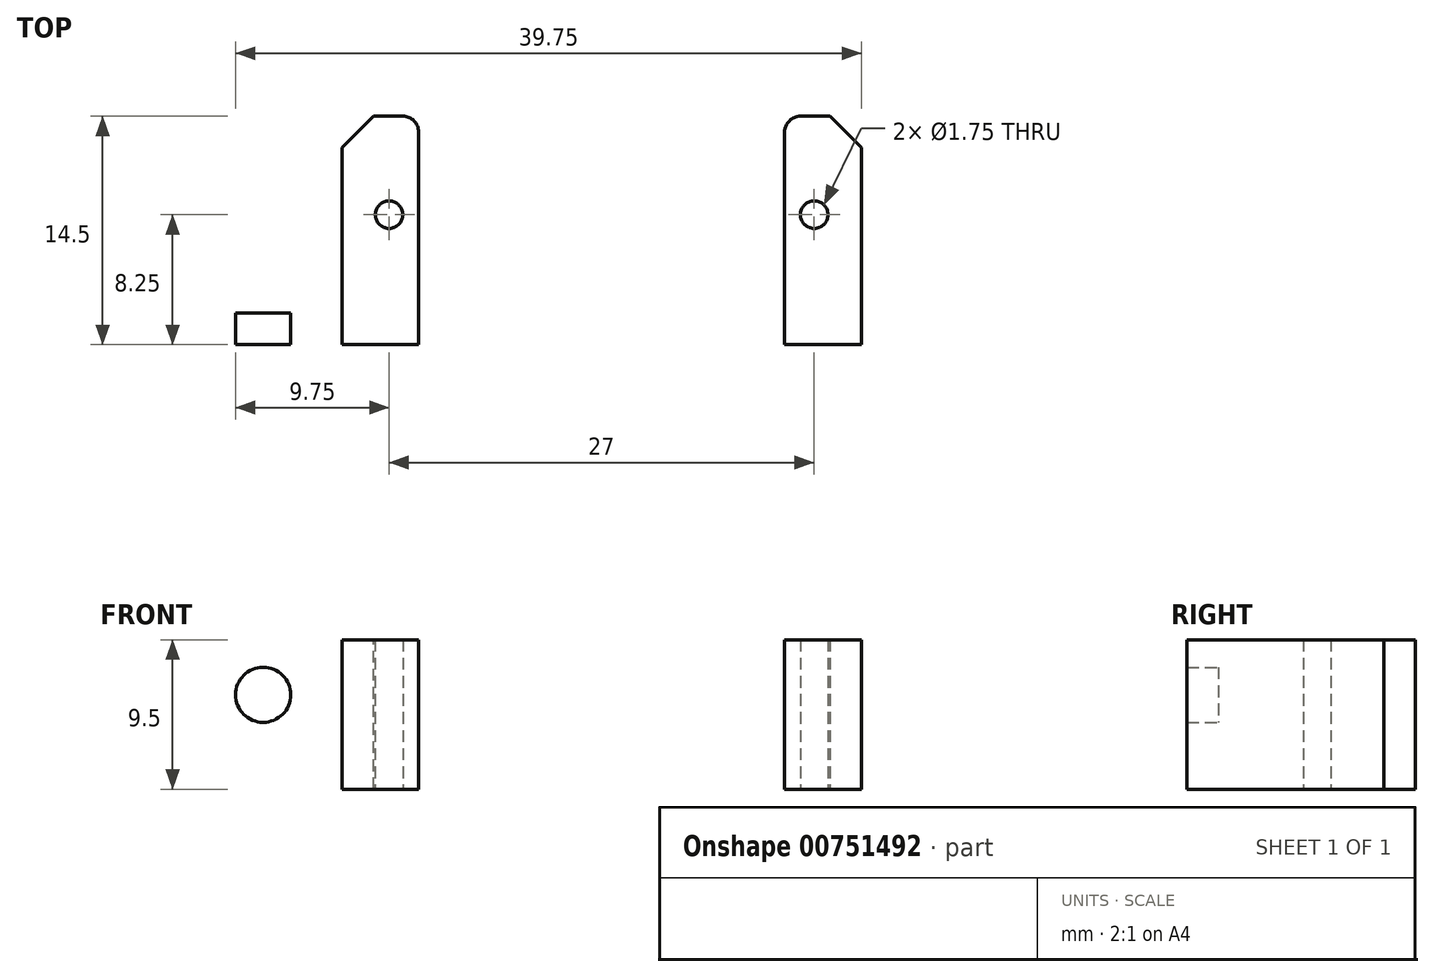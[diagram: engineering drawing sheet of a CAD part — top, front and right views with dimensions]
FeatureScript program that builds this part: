
annotation { "Feature Type Name" : "Feature", "Feature Type Description" : "" }
export const myFeature = defineFeature(function(context is Context, id is Id, definition is map)
    precondition{}
    {
        {
            var Q0;
            Q0=qCreatedBy(makeId("Top.planeOp"),FACE);
            var sketch = newSketch(context, id + "F0", { "sketchPlane" : qUnion([Q0])});
            skLineSegment(sketch, "E0.bottom", {"start": v(-16.5, 7.25) * mm, "end": v(16.5, 7.25) * mm});
            skLineSegment(sketch, "E0.top", {"start": v(-16.5, -7.25) * mm, "end": v(16.5, -7.25) * mm});
            skLineSegment(sketch, "E0.left", {"start": v(-16.5, 7.25) * mm, "end": v(-16.5, -7.25) * mm});
            skLineSegment(sketch, "E0.right", {"start": v(16.5, 7.25) * mm, "end": v(16.5, -7.25) * mm});
            skPoint(sketch, "E0.middle", {"position": v(0, 0) * mm});
            skLineSegment(sketch, "E1.bottom", {"start": v(-16.5, -5.25) * mm, "end": v(-24.5, -5.25) * mm});
            skLineSegment(sketch, "E1.top", {"start": v(-16.5, -7.25) * mm, "end": v(-24.5, -7.25) * mm});
            skLineSegment(sketch, "E1.left", {"start": v(-16.5, -5.25) * mm, "end": v(-16.5, -7.25) * mm});
            skLineSegment(sketch, "E1.right", {"start": v(-24.5, -5.25) * mm, "end": v(-24.5, -7.25) * mm});
            skLineSegment(sketch, "E2.MirrorCS", {"start": v(16.5, -5.25) * mm, "end": v(24.5, -5.25) * mm});
            skLineSegment(sketch, "E3.MirrorCS", {"start": v(16.5, -7.25) * mm, "end": v(24.5, -7.25) * mm});
            skLineSegment(sketch, "E4.MirrorCS", {"start": v(24.5, -5.25) * mm, "end": v(24.5, -7.25) * mm});
            skLineSegment(sketch, "E5.bottom", {"start": v(-11.62, 7.25) * mm, "end": v(11.62, 7.25) * mm});
            skLineSegment(sketch, "E5.top", {"start": v(-11.62, -5.25) * mm, "end": v(11.62, -5.25) * mm});
            skLineSegment(sketch, "E5.left", {"start": v(-11.62, 7.25) * mm, "end": v(-11.62, -5.25) * mm});
            skLineSegment(sketch, "E5.right", {"start": v(11.62, 7.25) * mm, "end": v(11.62, -5.25) * mm});
            skLineSegment(sketch, "E6", {"start": v(-11.62, -5.25) * mm, "end": v(-16.5, -5.25) * mm});
            skLineSegment(sketch, "E7", {"start": v(11.62, -5.25) * mm, "end": v(16.5, -5.25) * mm});
            skCircle(sketch, "E8", {"center": v(-13.5, 1) * mm, "radius": 0.88 * mm});
            skCircle(sketch, "E9.MirrorC", {"center": v(13.5, 1) * mm, "radius": 0.88 * mm});
            skSolve(sketch);
        }
        {
            var Q0;
            {var subQ1=sQuery(id+"F0.wireOp",EDGE,"E0.top");Q0=makeQuery(id+"F0.imprint","IMPRINT",FACE,{"disambiguationData":[TD([[makeQuery(id+"F0.imprint","IMPRINT",EDGE,{"derivedFrom":subQ1}),1.0]])]});}
            var Q1;
            Q1=makeQuery(id+"F0.imprint","IMPRINT",FACE,{"disambiguationData":[TD([[makeQuery(id+"F0.imprint","IMPRINT",EDGE,{"derivedFrom":sQuery(id+"F0.wireOp",EDGE,"E1.bottom")}),1.0]])]});
            var Q2;
            {var subQ2=sQuery(id+"F0.wireOp",EDGE,"E2.MirrorCS");Q2=makeQuery(id+"F0.imprint","IMPRINT",FACE,{"disambiguationData":[TD([[makeQuery(id+"F0.imprint","IMPRINT",EDGE,{"derivedFrom":subQ2}),-1.0]])]});}
            extrude(context, id + "F1", {"entities" : qUnion([Q0, Q1, Q2]), "depth" : 12 * mm, "offsetDistance" : 25 * mm});
        }
        {
            var Q0;
            {var subQ0=sQuery(id+"F0.wireOp",EDGE,"E0.left");Q0=makeQuery(id+"F0.imprint","IMPRINT",FACE,{"disambiguationData":[TD([[makeQuery(id+"F0.imprint","IMPRINT",EDGE,{"derivedFrom":subQ0}),1.0]])]});}
            var Q1;
            {var subQ4=sQuery(id+"F0.wireOp",EDGE,"E5.right");Q1=makeQuery(id+"F0.imprint","IMPRINT",FACE,{"disambiguationData":[TD([[makeQuery(id+"F0.imprint","IMPRINT",EDGE,{"derivedFrom":subQ4}),1.0]])]});}
            extrude(context, id + "F2", {"entities" : qUnion([Q0, Q1]), "operationType" : NewBodyOperationType.ADD, "depth" : 9.5 * mm, "offsetDistance" : 25 * mm});
        }
        {
            var Q0;
            Q0=makeQuery(id+"F1.opExtrude","SWEPT_EDGE",EDGE,{"disambiguationData":[OSD([sQuery(id+"F0.wireOp",EDGE,"E0.bottom"),sQuery(id+"F0.wireOp",EDGE,"E0.left")])]});
            var Q1;
            Q1=makeQuery(id+"F1.opExtrude","SWEPT_EDGE",EDGE,{"disambiguationData":[OSD([sQuery(id+"F0.wireOp",EDGE,"E0.bottom"),sQuery(id+"F0.wireOp",EDGE,"E0.right")])]});
            var Q2;
            Q2=makeQuery(id+"F1.opExtrude","CAP_EDGE",EDGE,{"disambiguationData":[OSD([sQuery(id+"F0.wireOp",EDGE,"E1.right")])],"isStart":false});
            var Q3;
            Q3=makeQuery(id+"F1.opExtrude","CAP_EDGE",EDGE,{"disambiguationData":[OSD([sQuery(id+"F0.wireOp",EDGE,"E1.right")])],"isStart":true});
            var Q4;
            Q4=makeQuery(id+"F1.opExtrude","CAP_EDGE",EDGE,{"disambiguationData":[OSD([sQuery(id+"F0.wireOp",EDGE,"E4.MirrorCS")])],"isStart":false});
            var Q5;
            Q5=makeQuery(id+"F1.opExtrude","CAP_EDGE",EDGE,{"disambiguationData":[OSD([sQuery(id+"F0.wireOp",EDGE,"E4.MirrorCS")])],"isStart":true});
            var Q6;
            Q6=makeQuery(id+"F2.opExtrude","SWEPT_EDGE",EDGE,{"disambiguationData":[OSD([sQuery(id+"F0.wireOp",EDGE,"E0.bottom"),sQuery(id+"F0.wireOp",EDGE,"E0.left")])]});
            var Q7;
            Q7=makeQuery(id+"F2.opExtrude","SWEPT_EDGE",EDGE,{"disambiguationData":[OSD([sQuery(id+"F0.wireOp",EDGE,"E0.bottom"),sQuery(id+"F0.wireOp",EDGE,"E0.right")])]});
            var Q8;
            Q8=makeQuery(id+"F2.opExtrude","SWEPT_EDGE",EDGE,{"disambiguationData":[OSD([sQuery(id+"F0.wireOp",EDGE,"E0.left"),sQuery(id+"F0.wireOp",EDGE,"E1.bottom"),sQuery(id+"F0.wireOp",EDGE,"E1.left"),sQuery(id+"F0.wireOp",EDGE,"E6")])]});
            var Q9;
            Q9=makeQuery(id+"F2.opExtrude","SWEPT_EDGE",EDGE,{"disambiguationData":[OSD([sQuery(id+"F0.wireOp",EDGE,"E0.right"),sQuery(id+"F0.wireOp",EDGE,"E2.MirrorCS"),sQuery(id+"F0.wireOp",EDGE,"E7")])]});
            chamfer(context, id + "F3", {"entities" : qUnion([Q0, Q1, Q2, Q3, Q4, Q5, Q6, Q7, Q8, Q9]), "width" : 2 * mm, "tangentPropagation" : true});
        }
        {
            var Q0;
            Q0=makeQuery(id+"F1.opExtrude","SWEPT_FACE",FACE,{"disambiguationData":[OSD([sQuery(id+"F0.wireOp",EDGE,"E1.bottom")])]});
            var sketch = newSketch(context, id + "F4", { "sketchPlane" : qUnion([Q0])});
            skCircle(sketch, "E10", {"center": v(-21.5, 6) * mm, "radius": 1.75 * mm});
            skLineSegment(sketch, "E11", {"start": v(-21.5, 6) * mm, "end": v(-24.5, 6) * mm, "construction": true});
            skLineSegment(sketch, "E12", {"start": v(-21.5, 6) * mm, "end": v(-18.5, 6) * mm, "construction": true});
            skCircle(sketch, "E13.MirrorC", {"center": v(21.5, 6) * mm, "radius": 1.75 * mm});
            skSolve(sketch);
        }
        {
            var Q0;
            Q0=makeQuery(id+"F4.imprint","IMPRINT",FACE,{"disambiguationData":[TD([[makeQuery(id+"F4.imprint","IMPRINT",EDGE,{"derivedFrom":sQuery(id+"F4.wireOp",EDGE,"E13.MirrorC")}),-1.0]])]});
            var Q1;
            Q1=makeQuery(id+"F4.imprint","IMPRINT",FACE,{"disambiguationData":[TD([[makeQuery(id+"F4.imprint","IMPRINT",EDGE,{"derivedFrom":sQuery(id+"F4.wireOp",EDGE,"E10")}),1.0]])]});
            var Q2;
            Q2=makeQuery(id+"F1.opExtrude","SWEPT_FACE",FACE,{"disambiguationData":[OSD([sQuery(id+"F0.wireOp",EDGE,"E0.top"),sQuery(id+"F0.wireOp",EDGE,"E1.top"),sQuery(id+"F0.wireOp",EDGE,"E3.MirrorCS")])]});
            extrude(context, id + "F5", {"entities" : qUnion([Q0, Q1]), "operationType" : NewBodyOperationType.REMOVE, "endBound" : BoundingType.UP_TO_SURFACE, "oppositeDirection" : true, "depth" : 25 * mm, "endBoundEntityFace" : qUnion([Q2]), "offsetDistance" : 25 * mm});
        }
        {
            var Q0;
            Q0=makeQuery(id+"F1.opExtrude","SWEPT_EDGE",EDGE,{"disambiguationData":[OSD([sQuery(id+"F0.wireOp",EDGE,"E5.top"),sQuery(id+"F0.wireOp",EDGE,"E5.right"),sQuery(id+"F0.wireOp",EDGE,"E7")])]});
            var Q1;
            Q1=makeQuery(id+"F1.opExtrude","SWEPT_EDGE",EDGE,{"disambiguationData":[OSD([sQuery(id+"F0.wireOp",EDGE,"E5.top"),sQuery(id+"F0.wireOp",EDGE,"E5.left"),sQuery(id+"F0.wireOp",EDGE,"E6")])]});
            var Q2;
            Q2=makeQuery(id+"F1.opExtrude","SWEPT_EDGE",EDGE,{"disambiguationData":[OSD([sQuery(id+"F0.wireOp",EDGE,"E0.bottom"),sQuery(id+"F0.wireOp",EDGE,"E5.bottom"),sQuery(id+"F0.wireOp",EDGE,"E5.left")])]});
            var Q3;
            Q3=makeQuery(id+"F1.opExtrude","SWEPT_EDGE",EDGE,{"disambiguationData":[OSD([sQuery(id+"F0.wireOp",EDGE,"E0.bottom"),sQuery(id+"F0.wireOp",EDGE,"E5.bottom"),sQuery(id+"F0.wireOp",EDGE,"E5.right")])]});
            var Q4;
            Q4=makeQuery(id+"F2.opExtrude","SWEPT_EDGE",EDGE,{"disambiguationData":[OSD([sQuery(id+"F0.wireOp",EDGE,"E0.bottom"),sQuery(id+"F0.wireOp",EDGE,"E5.bottom"),sQuery(id+"F0.wireOp",EDGE,"E5.left")])]});
            var Q5;
            Q5=makeQuery(id+"F2.opExtrude","SWEPT_EDGE",EDGE,{"disambiguationData":[OSD([sQuery(id+"F0.wireOp",EDGE,"E0.bottom"),sQuery(id+"F0.wireOp",EDGE,"E5.bottom"),sQuery(id+"F0.wireOp",EDGE,"E5.right")])]});
            var Q6;
            Q6=makeQuery(id+"F2.opExtrude","SWEPT_EDGE",EDGE,{"disambiguationData":[OSD([sQuery(id+"F0.wireOp",EDGE,"E5.top"),sQuery(id+"F0.wireOp",EDGE,"E5.left"),sQuery(id+"F0.wireOp",EDGE,"E6")])]});
            var Q7;
            Q7=makeQuery(id+"F2.opExtrude","SWEPT_EDGE",EDGE,{"disambiguationData":[OSD([sQuery(id+"F0.wireOp",EDGE,"E5.top"),sQuery(id+"F0.wireOp",EDGE,"E5.right"),sQuery(id+"F0.wireOp",EDGE,"E7")])]});
            fillet(context, id + "F6", {"entities" : qUnion([Q0, Q1, Q2, Q3, Q4, Q5, Q6, Q7]), "radius" : 1 * mm, "tangentPropagation" : true, "allowEdgeOverflow" : false});
        }
    });
